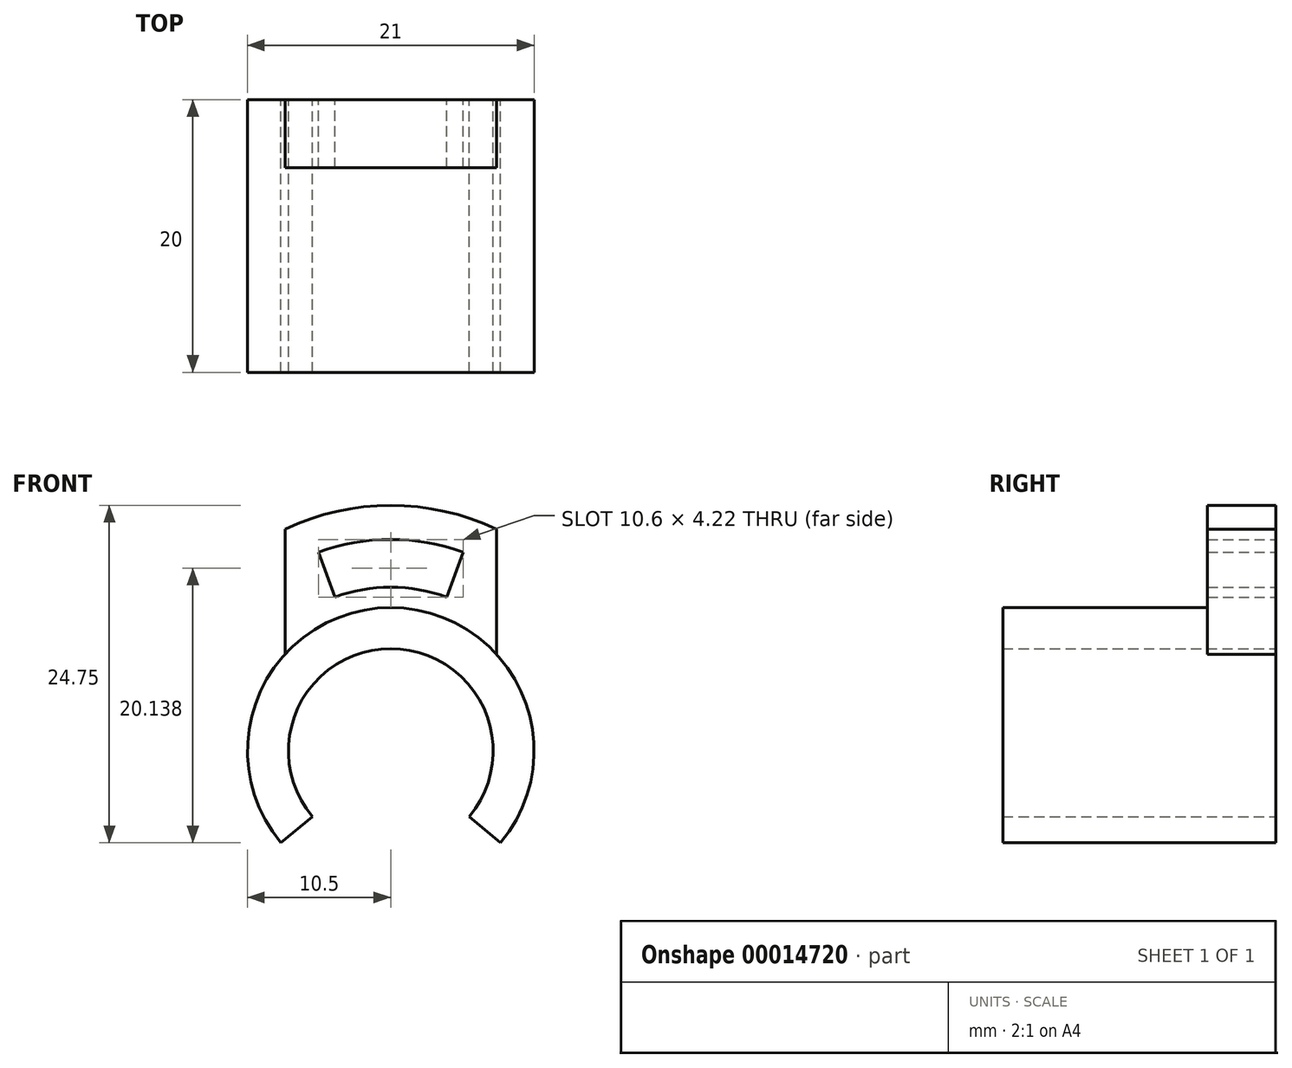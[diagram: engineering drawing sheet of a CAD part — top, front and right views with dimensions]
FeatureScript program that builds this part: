
annotation { "Feature Type Name" : "Feature", "Feature Type Description" : "" }
export const myFeature = defineFeature(function(context is Context, id is Id, definition is map)
    precondition{}
    {
        {
            var Q0;
            Q0=qCreatedBy(makeId("Front.planeOp"),FACE);
            var sketch = newSketch(context, id + "F0", { "sketchPlane" : qUnion([Q0])});
            skArc(sketch, "E0", {"start": v(5.75, -10.35) * mm, "mid": v(0, 1.97) * mm, "end": v(-5.75, -10.35) * mm});
            skArc(sketch, "E1", {"start": v(8.04, -12.28) * mm, "mid": v(0, 4.97) * mm, "end": v(-8.04, -12.28) * mm});
            skArc(sketch, "E2", {"start": v(5.3, 9.04) * mm, "mid": v(0, 9.97) * mm, "end": v(-5.3, 9.04) * mm});
            skArc(sketch, "E3", {"start": v(4.1, 5.75) * mm, "mid": v(0, 6.47) * mm, "end": v(-4.1, 5.75) * mm});
            skLineSegment(sketch, "E4", {"start": v(-5.75, -10.35) * mm, "end": v(-8.04, -12.28) * mm});
            skLineSegment(sketch, "E5", {"start": v(5.75, -10.35) * mm, "end": v(8.04, -12.28) * mm});
            skLineSegment(sketch, "E6", {"start": v(-4.1, 5.75) * mm, "end": v(-5.3, 9.04) * mm});
            skLineSegment(sketch, "E7.trimOffspring", {"start": v(0, 4.97) * mm, "end": v(0, 6.47) * mm});
            skLineSegment(sketch, "E8.trimOffspring", {"start": v(4.1, 5.75) * mm, "end": v(5.3, 9.04) * mm});
            skLineSegment(sketch, "E9", {"start": v(-7.75, 10.72) * mm, "end": v(-7.75, 1.55) * mm});
            skLineSegment(sketch, "E10", {"start": v(7.75, 10.72) * mm, "end": v(7.75, 1.55) * mm});
            skArc(sketch, "E11", {"start": v(7.75, 10.72) * mm, "mid": v(0, 12.47) * mm, "end": v(-7.75, 10.72) * mm});
            skSolve(sketch);
        }
        {
            var Q0;
            Q0=makeQuery(id+"F0.imprint","IMPRINT",FACE,{"disambiguationData":[TD([[makeQuery(id+"F0.imprint","IMPRINT",EDGE,{"derivedFrom":sQuery(id+"F0.wireOp",EDGE,"E0")}),-1.0]])]});
            extrude(context, id + "F1", {"entities" : qUnion([Q0]), "depth" : 20 * mm});
        }
        {
            var Q0;
            Q0=makeQuery(id+"F0.imprint","IMPRINT",FACE,{"disambiguationData":[TD([[makeQuery(id+"F0.imprint","IMPRINT",EDGE,{"derivedFrom":sQuery(id+"F0.wireOp",EDGE,"E2")}),-1.0]])]});
            extrude(context, id + "F2", {"entities" : qUnion([Q0]), "operationType" : NewBodyOperationType.ADD, "depth" : 5 * mm});
        }
    });
